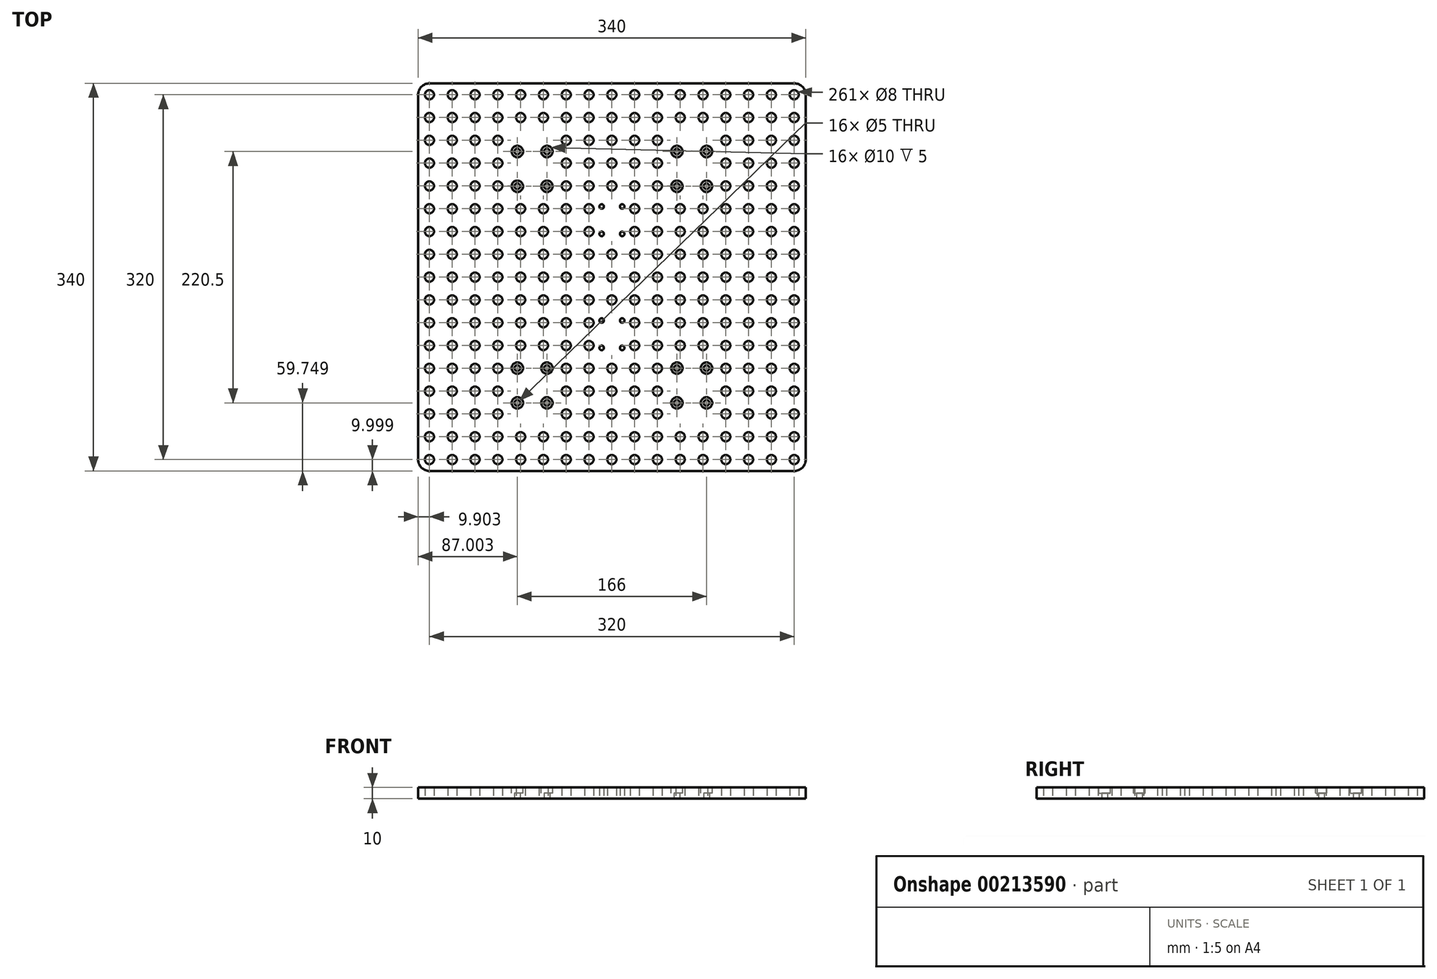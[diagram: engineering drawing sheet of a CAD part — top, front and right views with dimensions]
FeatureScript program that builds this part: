
annotation { "Feature Type Name" : "Feature", "Feature Type Description" : "" }
export const myFeature = defineFeature(function(context is Context, id is Id, definition is map)
    precondition{}
    {
        {
            var Q0;
            Q0=qCreatedBy(makeId("Top.planeOp"),FACE);
            var sketch = newSketch(context, id + "F0", { "sketchPlane" : qUnion([Q0])});
            skLineSegment(sketch, "E0", {"start": v(-202.87, 176.2) * mm, "end": v(-202.87, -163.8) * mm});
            skLineSegment(sketch, "E1", {"start": v(-202.87, -163.8) * mm, "end": v(137.13, -163.8) * mm});
            skLineSegment(sketch, "E2", {"start": v(137.13, -163.8) * mm, "end": v(137.13, 176.2) * mm});
            skLineSegment(sketch, "E3", {"start": v(137.13, 176.2) * mm, "end": v(-202.87, 176.2) * mm});
            skCircle(sketch, "E4", {"center": v(-192.97, -153.8) * mm, "radius": 4 * mm});
            skCircle(sketch, "E5.0.1.0", {"center": v(-192.97, -133.8) * mm, "radius": 4 * mm});
            skCircle(sketch, "E5.0.2.0", {"center": v(-192.97, -113.8) * mm, "radius": 4 * mm});
            skCircle(sketch, "E5.0.3.0", {"center": v(-192.97, -93.8) * mm, "radius": 4 * mm});
            skCircle(sketch, "E5.0.4.0", {"center": v(-192.97, -73.8) * mm, "radius": 4 * mm});
            skCircle(sketch, "E5.0.5.0", {"center": v(-192.97, -53.8) * mm, "radius": 4 * mm});
            skCircle(sketch, "E5.0.6.0", {"center": v(-192.97, -33.8) * mm, "radius": 4 * mm});
            skCircle(sketch, "E5.0.7.0", {"center": v(-192.97, -13.8) * mm, "radius": 4 * mm});
            skCircle(sketch, "E5.0.8.0", {"center": v(-192.97, 6.2) * mm, "radius": 4 * mm});
            skCircle(sketch, "E5.0.9.0", {"center": v(-192.97, 26.2) * mm, "radius": 4 * mm});
            skCircle(sketch, "E5.0.10.0", {"center": v(-192.97, 46.2) * mm, "radius": 4 * mm});
            skCircle(sketch, "E5.0.11.0", {"center": v(-192.97, 66.2) * mm, "radius": 4 * mm});
            skCircle(sketch, "E5.0.12.0", {"center": v(-192.97, 86.2) * mm, "radius": 4 * mm});
            skCircle(sketch, "E5.0.13.0", {"center": v(-192.97, 106.2) * mm, "radius": 4 * mm});
            skCircle(sketch, "E5.0.14.0", {"center": v(-192.97, 126.2) * mm, "radius": 4 * mm});
            skCircle(sketch, "E5.0.15.0", {"center": v(-192.97, 146.2) * mm, "radius": 4 * mm});
            skCircle(sketch, "E5.0.16.0", {"center": v(-192.97, 166.2) * mm, "radius": 4 * mm});
            skLineSegment(sketch, "E5.direction1", {"start": v(-192.97, -153.8) * mm, "end": v(-172.97, -153.8) * mm, "construction": true});
            skLineSegment(sketch, "E5.direction2", {"start": v(-192.97, -153.8) * mm, "end": v(-192.97, -133.8) * mm, "construction": true});
            skCircle(sketch, "E6", {"center": v(24.13, -73.55) * mm, "radius": 2.5 * mm});
            skCircle(sketch, "E7", {"center": v(50.13, -73.55) * mm, "radius": 2.5 * mm});
            skCircle(sketch, "E8", {"center": v(24.13, -104.05) * mm, "radius": 2.5 * mm});
            skCircle(sketch, "E9", {"center": v(50.13, -104.05) * mm, "radius": 2.5 * mm});
            skLineSegment(sketch, "E10", {"start": v(24.13, -73.55) * mm, "end": v(50.13, -104.05) * mm, "construction": true});
            skLineSegment(sketch, "E11", {"start": v(37.13, -88.8) * mm, "end": v(50.13, -104.05) * mm, "construction": true});
            skCircle(sketch, "E12", {"center": v(24.13, 116.45) * mm, "radius": 2.5 * mm});
            skCircle(sketch, "E13", {"center": v(50.13, 116.45) * mm, "radius": 2.5 * mm});
            skCircle(sketch, "E14", {"center": v(24.13, 85.95) * mm, "radius": 2.5 * mm});
            skCircle(sketch, "E15", {"center": v(50.13, 85.95) * mm, "radius": 2.5 * mm});
            skLineSegment(sketch, "E16", {"start": v(24.13, 116.45) * mm, "end": v(50.13, 85.95) * mm, "construction": true});
            skLineSegment(sketch, "E17", {"start": v(37.13, 101.2) * mm, "end": v(50.13, 85.95) * mm, "construction": true});
            skCircle(sketch, "E18", {"center": v(-115.87, 116.45) * mm, "radius": 2.5 * mm});
            skCircle(sketch, "E19", {"center": v(-89.87, 116.45) * mm, "radius": 2.5 * mm});
            skCircle(sketch, "E20", {"center": v(-115.87, 85.95) * mm, "radius": 2.5 * mm});
            skCircle(sketch, "E21", {"center": v(-89.87, 85.95) * mm, "radius": 2.5 * mm});
            skLineSegment(sketch, "E22", {"start": v(-115.87, 116.45) * mm, "end": v(-89.87, 85.95) * mm, "construction": true});
            skLineSegment(sketch, "E23", {"start": v(-102.87, 101.2) * mm, "end": v(-89.87, 85.95) * mm, "construction": true});
            skCircle(sketch, "E24", {"center": v(-115.87, -73.55) * mm, "radius": 2.5 * mm});
            skCircle(sketch, "E25", {"center": v(-89.87, -73.55) * mm, "radius": 2.5 * mm});
            skCircle(sketch, "E26", {"center": v(-115.87, -104.05) * mm, "radius": 2.5 * mm});
            skCircle(sketch, "E27", {"center": v(-89.87, -104.05) * mm, "radius": 2.5 * mm});
            skLineSegment(sketch, "E28", {"start": v(-115.87, -73.55) * mm, "end": v(-89.87, -104.05) * mm, "construction": true});
            skLineSegment(sketch, "E29", {"start": v(-102.87, -88.8) * mm, "end": v(-89.87, -104.05) * mm, "construction": true});
            skCircle(sketch, "E30.0.1.0", {"center": v(-172.97, -153.8) * mm, "radius": 4 * mm});
            skCircle(sketch, "E30.0.1.1", {"center": v(-172.97, -133.8) * mm, "radius": 4 * mm});
            skCircle(sketch, "E30.0.1.2", {"center": v(-172.97, -113.8) * mm, "radius": 4 * mm});
            skCircle(sketch, "E30.0.1.3", {"center": v(-172.97, -93.8) * mm, "radius": 4 * mm});
            skCircle(sketch, "E30.0.1.4", {"center": v(-172.97, -73.8) * mm, "radius": 4 * mm});
            skCircle(sketch, "E30.0.1.5", {"center": v(-172.97, -53.8) * mm, "radius": 4 * mm});
            skCircle(sketch, "E30.0.1.6", {"center": v(-172.97, -33.8) * mm, "radius": 4 * mm});
            skCircle(sketch, "E30.0.1.7", {"center": v(-172.97, -13.8) * mm, "radius": 4 * mm});
            skCircle(sketch, "E30.0.1.8", {"center": v(-172.97, 6.2) * mm, "radius": 4 * mm});
            skCircle(sketch, "E30.0.1.9", {"center": v(-172.97, 26.2) * mm, "radius": 4 * mm});
            skCircle(sketch, "E30.0.1.10", {"center": v(-172.97, 46.2) * mm, "radius": 4 * mm});
            skCircle(sketch, "E30.0.1.11", {"center": v(-172.97, 66.2) * mm, "radius": 4 * mm});
            skCircle(sketch, "E30.0.1.12", {"center": v(-172.97, 86.2) * mm, "radius": 4 * mm});
            skCircle(sketch, "E30.0.1.13", {"center": v(-172.97, 106.2) * mm, "radius": 4 * mm});
            skCircle(sketch, "E30.0.1.14", {"center": v(-172.97, 126.2) * mm, "radius": 4 * mm});
            skCircle(sketch, "E30.0.1.15", {"center": v(-172.97, 146.2) * mm, "radius": 4 * mm});
            skCircle(sketch, "E30.0.1.16", {"center": v(-172.97, 166.2) * mm, "radius": 4 * mm});
            skCircle(sketch, "E30.0.2.0", {"center": v(-152.97, -153.8) * mm, "radius": 4 * mm});
            skCircle(sketch, "E30.0.2.1", {"center": v(-152.97, -133.8) * mm, "radius": 4 * mm});
            skCircle(sketch, "E30.0.2.2", {"center": v(-152.97, -113.8) * mm, "radius": 4 * mm});
            skCircle(sketch, "E30.0.2.3", {"center": v(-152.97, -93.8) * mm, "radius": 4 * mm});
            skCircle(sketch, "E30.0.2.4", {"center": v(-152.97, -73.8) * mm, "radius": 4 * mm});
            skCircle(sketch, "E30.0.2.5", {"center": v(-152.97, -53.8) * mm, "radius": 4 * mm});
            skCircle(sketch, "E30.0.2.6", {"center": v(-152.97, -33.8) * mm, "radius": 4 * mm});
            skCircle(sketch, "E30.0.2.7", {"center": v(-152.97, -13.8) * mm, "radius": 4 * mm});
            skCircle(sketch, "E30.0.2.8", {"center": v(-152.97, 6.2) * mm, "radius": 4 * mm});
            skCircle(sketch, "E30.0.2.9", {"center": v(-152.97, 26.2) * mm, "radius": 4 * mm});
            skCircle(sketch, "E30.0.2.10", {"center": v(-152.97, 46.2) * mm, "radius": 4 * mm});
            skCircle(sketch, "E30.0.2.11", {"center": v(-152.97, 66.2) * mm, "radius": 4 * mm});
            skCircle(sketch, "E30.0.2.12", {"center": v(-152.97, 86.2) * mm, "radius": 4 * mm});
            skCircle(sketch, "E30.0.2.13", {"center": v(-152.97, 106.2) * mm, "radius": 4 * mm});
            skCircle(sketch, "E30.0.2.14", {"center": v(-152.97, 126.2) * mm, "radius": 4 * mm});
            skCircle(sketch, "E30.0.2.15", {"center": v(-152.97, 146.2) * mm, "radius": 4 * mm});
            skCircle(sketch, "E30.0.2.16", {"center": v(-152.97, 166.2) * mm, "radius": 4 * mm});
            skCircle(sketch, "E30.0.3.0", {"center": v(-132.97, -153.8) * mm, "radius": 4 * mm});
            skCircle(sketch, "E30.0.3.1", {"center": v(-132.97, -133.8) * mm, "radius": 4 * mm});
            skCircle(sketch, "E30.0.3.2", {"center": v(-132.97, -113.8) * mm, "radius": 4 * mm});
            skCircle(sketch, "E30.0.3.3", {"center": v(-132.97, -93.8) * mm, "radius": 4 * mm});
            skCircle(sketch, "E30.0.3.4", {"center": v(-132.97, -73.8) * mm, "radius": 4 * mm});
            skCircle(sketch, "E30.0.3.5", {"center": v(-132.97, -53.8) * mm, "radius": 4 * mm});
            skCircle(sketch, "E30.0.3.6", {"center": v(-132.97, -33.8) * mm, "radius": 4 * mm});
            skCircle(sketch, "E30.0.3.7", {"center": v(-132.97, -13.8) * mm, "radius": 4 * mm});
            skCircle(sketch, "E30.0.3.8", {"center": v(-132.97, 6.2) * mm, "radius": 4 * mm});
            skCircle(sketch, "E30.0.3.9", {"center": v(-132.97, 26.2) * mm, "radius": 4 * mm});
            skCircle(sketch, "E30.0.3.10", {"center": v(-132.97, 46.2) * mm, "radius": 4 * mm});
            skCircle(sketch, "E30.0.3.11", {"center": v(-132.97, 66.2) * mm, "radius": 4 * mm});
            skCircle(sketch, "E30.0.3.12", {"center": v(-132.97, 86.2) * mm, "radius": 4 * mm});
            skCircle(sketch, "E30.0.3.13", {"center": v(-132.97, 106.2) * mm, "radius": 4 * mm});
            skCircle(sketch, "E30.0.3.14", {"center": v(-132.97, 126.2) * mm, "radius": 4 * mm});
            skCircle(sketch, "E30.0.3.15", {"center": v(-132.97, 146.2) * mm, "radius": 4 * mm});
            skCircle(sketch, "E30.0.3.16", {"center": v(-132.97, 166.2) * mm, "radius": 4 * mm});
            skCircle(sketch, "E30.0.4.0", {"center": v(-112.97, -153.8) * mm, "radius": 4 * mm});
            skCircle(sketch, "E30.0.4.1", {"center": v(-112.97, -133.8) * mm, "radius": 4 * mm});
            skCircle(sketch, "E30.0.4.5", {"center": v(-112.97, -53.8) * mm, "radius": 4 * mm});
            skCircle(sketch, "E30.0.4.6", {"center": v(-112.97, -33.8) * mm, "radius": 4 * mm});
            skCircle(sketch, "E30.0.4.7", {"center": v(-112.97, -13.8) * mm, "radius": 4 * mm});
            skCircle(sketch, "E30.0.4.8", {"center": v(-112.97, 6.2) * mm, "radius": 4 * mm});
            skCircle(sketch, "E30.0.4.9", {"center": v(-112.97, 26.2) * mm, "radius": 4 * mm});
            skCircle(sketch, "E30.0.4.10", {"center": v(-112.97, 46.2) * mm, "radius": 4 * mm});
            skCircle(sketch, "E30.0.4.11", {"center": v(-112.97, 66.2) * mm, "radius": 4 * mm});
            skCircle(sketch, "E30.0.4.15", {"center": v(-112.97, 146.2) * mm, "radius": 4 * mm});
            skCircle(sketch, "E30.0.4.16", {"center": v(-112.97, 166.2) * mm, "radius": 4 * mm});
            skCircle(sketch, "E30.0.5.0", {"center": v(-92.97, -153.8) * mm, "radius": 4 * mm});
            skCircle(sketch, "E30.0.5.1", {"center": v(-92.97, -133.8) * mm, "radius": 4 * mm});
            skCircle(sketch, "E30.0.5.5", {"center": v(-92.97, -53.8) * mm, "radius": 4 * mm});
            skCircle(sketch, "E30.0.5.6", {"center": v(-92.97, -33.8) * mm, "radius": 4 * mm});
            skCircle(sketch, "E30.0.5.7", {"center": v(-92.97, -13.8) * mm, "radius": 4 * mm});
            skCircle(sketch, "E30.0.5.8", {"center": v(-92.97, 6.2) * mm, "radius": 4 * mm});
            skCircle(sketch, "E30.0.5.9", {"center": v(-92.97, 26.2) * mm, "radius": 4 * mm});
            skCircle(sketch, "E30.0.5.10", {"center": v(-92.97, 46.2) * mm, "radius": 4 * mm});
            skCircle(sketch, "E30.0.5.11", {"center": v(-92.97, 66.2) * mm, "radius": 4 * mm});
            skCircle(sketch, "E30.0.5.15", {"center": v(-92.97, 146.2) * mm, "radius": 4 * mm});
            skCircle(sketch, "E30.0.5.16", {"center": v(-92.97, 166.2) * mm, "radius": 4 * mm});
            skCircle(sketch, "E30.0.6.0", {"center": v(-72.97, -153.8) * mm, "radius": 4 * mm});
            skCircle(sketch, "E30.0.6.1", {"center": v(-72.97, -133.8) * mm, "radius": 4 * mm});
            skCircle(sketch, "E30.0.6.2", {"center": v(-72.97, -113.8) * mm, "radius": 4 * mm});
            skCircle(sketch, "E30.0.6.3", {"center": v(-72.97, -93.8) * mm, "radius": 4 * mm});
            skCircle(sketch, "E30.0.6.4", {"center": v(-72.97, -73.8) * mm, "radius": 4 * mm});
            skCircle(sketch, "E30.0.6.5", {"center": v(-72.97, -53.8) * mm, "radius": 4 * mm});
            skCircle(sketch, "E30.0.6.6", {"center": v(-72.97, -33.8) * mm, "radius": 4 * mm});
            skCircle(sketch, "E30.0.6.7", {"center": v(-72.97, -13.8) * mm, "radius": 4 * mm});
            skCircle(sketch, "E30.0.6.8", {"center": v(-72.97, 6.2) * mm, "radius": 4 * mm});
            skCircle(sketch, "E30.0.6.9", {"center": v(-72.97, 26.2) * mm, "radius": 4 * mm});
            skCircle(sketch, "E30.0.6.10", {"center": v(-72.97, 46.2) * mm, "radius": 4 * mm});
            skCircle(sketch, "E30.0.6.11", {"center": v(-72.97, 66.2) * mm, "radius": 4 * mm});
            skCircle(sketch, "E30.0.6.12", {"center": v(-72.97, 86.2) * mm, "radius": 4 * mm});
            skCircle(sketch, "E30.0.6.13", {"center": v(-72.97, 106.2) * mm, "radius": 4 * mm});
            skCircle(sketch, "E30.0.6.14", {"center": v(-72.97, 126.2) * mm, "radius": 4 * mm});
            skCircle(sketch, "E30.0.6.15", {"center": v(-72.97, 146.2) * mm, "radius": 4 * mm});
            skCircle(sketch, "E30.0.6.16", {"center": v(-72.97, 166.2) * mm, "radius": 4 * mm});
            skCircle(sketch, "E30.0.7.0", {"center": v(-52.97, -153.8) * mm, "radius": 4 * mm});
            skCircle(sketch, "E30.0.7.1", {"center": v(-52.97, -133.8) * mm, "radius": 4 * mm});
            skCircle(sketch, "E30.0.7.2", {"center": v(-52.97, -113.8) * mm, "radius": 4 * mm});
            skCircle(sketch, "E30.0.7.3", {"center": v(-52.97, -93.8) * mm, "radius": 4 * mm});
            skCircle(sketch, "E30.0.7.4", {"center": v(-52.97, -73.8) * mm, "radius": 4 * mm});
            skCircle(sketch, "E30.0.7.5", {"center": v(-52.97, -53.8) * mm, "radius": 4 * mm});
            skCircle(sketch, "E30.0.7.6", {"center": v(-52.97, -33.8) * mm, "radius": 4 * mm});
            skCircle(sketch, "E30.0.7.7", {"center": v(-52.97, -13.8) * mm, "radius": 4 * mm});
            skCircle(sketch, "E30.0.7.8", {"center": v(-52.97, 6.2) * mm, "radius": 4 * mm});
            skCircle(sketch, "E30.0.7.9", {"center": v(-52.97, 26.2) * mm, "radius": 4 * mm});
            skCircle(sketch, "E30.0.7.10", {"center": v(-52.97, 46.2) * mm, "radius": 4 * mm});
            skCircle(sketch, "E30.0.7.11", {"center": v(-52.97, 66.2) * mm, "radius": 4 * mm});
            skCircle(sketch, "E30.0.7.12", {"center": v(-52.97, 86.2) * mm, "radius": 4 * mm});
            skCircle(sketch, "E30.0.7.13", {"center": v(-52.97, 106.2) * mm, "radius": 4 * mm});
            skCircle(sketch, "E30.0.7.14", {"center": v(-52.97, 126.2) * mm, "radius": 4 * mm});
            skCircle(sketch, "E30.0.7.15", {"center": v(-52.97, 146.2) * mm, "radius": 4 * mm});
            skCircle(sketch, "E30.0.7.16", {"center": v(-52.97, 166.2) * mm, "radius": 4 * mm});
            skCircle(sketch, "E30.0.8.0", {"center": v(-32.97, -153.8) * mm, "radius": 4 * mm});
            skCircle(sketch, "E30.0.8.1", {"center": v(-32.97, -133.8) * mm, "radius": 4 * mm});
            skCircle(sketch, "E30.0.8.2", {"center": v(-32.97, -113.8) * mm, "radius": 4 * mm});
            skCircle(sketch, "E30.0.8.3", {"center": v(-32.97, -93.8) * mm, "radius": 4 * mm});
            skCircle(sketch, "E30.0.8.4", {"center": v(-32.97, -73.8) * mm, "radius": 4 * mm});
            skCircle(sketch, "E30.0.8.7", {"center": v(-32.97, -13.8) * mm, "radius": 4 * mm});
            skCircle(sketch, "E30.0.8.8", {"center": v(-32.97, 6.2) * mm, "radius": 4 * mm});
            skCircle(sketch, "E30.0.8.9", {"center": v(-32.97, 26.2) * mm, "radius": 4 * mm});
            skCircle(sketch, "E30.0.8.12", {"center": v(-32.97, 86.2) * mm, "radius": 4 * mm});
            skCircle(sketch, "E30.0.8.13", {"center": v(-32.97, 106.2) * mm, "radius": 4 * mm});
            skCircle(sketch, "E30.0.8.14", {"center": v(-32.97, 126.2) * mm, "radius": 4 * mm});
            skCircle(sketch, "E30.0.8.15", {"center": v(-32.97, 146.2) * mm, "radius": 4 * mm});
            skCircle(sketch, "E30.0.8.16", {"center": v(-32.97, 166.2) * mm, "radius": 4 * mm});
            skCircle(sketch, "E30.0.9.0", {"center": v(-12.97, -153.8) * mm, "radius": 4 * mm});
            skCircle(sketch, "E30.0.9.1", {"center": v(-12.97, -133.8) * mm, "radius": 4 * mm});
            skCircle(sketch, "E30.0.9.2", {"center": v(-12.97, -113.8) * mm, "radius": 4 * mm});
            skCircle(sketch, "E30.0.9.3", {"center": v(-12.97, -93.8) * mm, "radius": 4 * mm});
            skCircle(sketch, "E30.0.9.4", {"center": v(-12.97, -73.8) * mm, "radius": 4 * mm});
            skCircle(sketch, "E30.0.9.5", {"center": v(-12.97, -53.8) * mm, "radius": 4 * mm});
            skCircle(sketch, "E30.0.9.6", {"center": v(-12.97, -33.8) * mm, "radius": 4 * mm});
            skCircle(sketch, "E30.0.9.7", {"center": v(-12.97, -13.8) * mm, "radius": 4 * mm});
            skCircle(sketch, "E30.0.9.8", {"center": v(-12.97, 6.2) * mm, "radius": 4 * mm});
            skCircle(sketch, "E30.0.9.9", {"center": v(-12.97, 26.2) * mm, "radius": 4 * mm});
            skCircle(sketch, "E30.0.9.10", {"center": v(-12.97, 46.2) * mm, "radius": 4 * mm});
            skCircle(sketch, "E30.0.9.11", {"center": v(-12.97, 66.2) * mm, "radius": 4 * mm});
            skCircle(sketch, "E30.0.9.12", {"center": v(-12.97, 86.2) * mm, "radius": 4 * mm});
            skCircle(sketch, "E30.0.9.13", {"center": v(-12.97, 106.2) * mm, "radius": 4 * mm});
            skCircle(sketch, "E30.0.9.14", {"center": v(-12.97, 126.2) * mm, "radius": 4 * mm});
            skCircle(sketch, "E30.0.9.15", {"center": v(-12.97, 146.2) * mm, "radius": 4 * mm});
            skCircle(sketch, "E30.0.9.16", {"center": v(-12.97, 166.2) * mm, "radius": 4 * mm});
            skCircle(sketch, "E30.0.10.0", {"center": v(7.03, -153.8) * mm, "radius": 4 * mm});
            skCircle(sketch, "E30.0.10.1", {"center": v(7.03, -133.8) * mm, "radius": 4 * mm});
            skCircle(sketch, "E30.0.10.2", {"center": v(7.03, -113.8) * mm, "radius": 4 * mm});
            skCircle(sketch, "E30.0.10.3", {"center": v(7.03, -93.8) * mm, "radius": 4 * mm});
            skCircle(sketch, "E30.0.10.4", {"center": v(7.03, -73.8) * mm, "radius": 4 * mm});
            skCircle(sketch, "E30.0.10.5", {"center": v(7.03, -53.8) * mm, "radius": 4 * mm});
            skCircle(sketch, "E30.0.10.6", {"center": v(7.03, -33.8) * mm, "radius": 4 * mm});
            skCircle(sketch, "E30.0.10.7", {"center": v(7.03, -13.8) * mm, "radius": 4 * mm});
            skCircle(sketch, "E30.0.10.8", {"center": v(7.03, 6.2) * mm, "radius": 4 * mm});
            skCircle(sketch, "E30.0.10.9", {"center": v(7.03, 26.2) * mm, "radius": 4 * mm});
            skCircle(sketch, "E30.0.10.10", {"center": v(7.03, 46.2) * mm, "radius": 4 * mm});
            skCircle(sketch, "E30.0.10.11", {"center": v(7.03, 66.2) * mm, "radius": 4 * mm});
            skCircle(sketch, "E30.0.10.12", {"center": v(7.03, 86.2) * mm, "radius": 4 * mm});
            skCircle(sketch, "E30.0.10.13", {"center": v(7.03, 106.2) * mm, "radius": 4 * mm});
            skCircle(sketch, "E30.0.10.14", {"center": v(7.03, 126.2) * mm, "radius": 4 * mm});
            skCircle(sketch, "E30.0.10.15", {"center": v(7.03, 146.2) * mm, "radius": 4 * mm});
            skCircle(sketch, "E30.0.10.16", {"center": v(7.03, 166.2) * mm, "radius": 4 * mm});
            skCircle(sketch, "E30.0.11.0", {"center": v(27.03, -153.8) * mm, "radius": 4 * mm});
            skCircle(sketch, "E30.0.11.1", {"center": v(27.03, -133.8) * mm, "radius": 4 * mm});
            skCircle(sketch, "E30.0.11.5", {"center": v(27.03, -53.8) * mm, "radius": 4 * mm});
            skCircle(sketch, "E30.0.11.6", {"center": v(27.03, -33.8) * mm, "radius": 4 * mm});
            skCircle(sketch, "E30.0.11.7", {"center": v(27.03, -13.8) * mm, "radius": 4 * mm});
            skCircle(sketch, "E30.0.11.8", {"center": v(27.03, 6.2) * mm, "radius": 4 * mm});
            skCircle(sketch, "E30.0.11.9", {"center": v(27.03, 26.2) * mm, "radius": 4 * mm});
            skCircle(sketch, "E30.0.11.10", {"center": v(27.03, 46.2) * mm, "radius": 4 * mm});
            skCircle(sketch, "E30.0.11.11", {"center": v(27.03, 66.2) * mm, "radius": 4 * mm});
            skCircle(sketch, "E30.0.11.15", {"center": v(27.03, 146.2) * mm, "radius": 4 * mm});
            skCircle(sketch, "E30.0.11.16", {"center": v(27.03, 166.2) * mm, "radius": 4 * mm});
            skCircle(sketch, "E30.0.12.0", {"center": v(47.03, -153.8) * mm, "radius": 4 * mm});
            skCircle(sketch, "E30.0.12.1", {"center": v(47.03, -133.8) * mm, "radius": 4 * mm});
            skCircle(sketch, "E30.0.12.5", {"center": v(47.03, -53.8) * mm, "radius": 4 * mm});
            skCircle(sketch, "E30.0.12.6", {"center": v(47.03, -33.8) * mm, "radius": 4 * mm});
            skCircle(sketch, "E30.0.12.7", {"center": v(47.03, -13.8) * mm, "radius": 4 * mm});
            skCircle(sketch, "E30.0.12.8", {"center": v(47.03, 6.2) * mm, "radius": 4 * mm});
            skCircle(sketch, "E30.0.12.9", {"center": v(47.03, 26.2) * mm, "radius": 4 * mm});
            skCircle(sketch, "E30.0.12.10", {"center": v(47.03, 46.2) * mm, "radius": 4 * mm});
            skCircle(sketch, "E30.0.12.11", {"center": v(47.03, 66.2) * mm, "radius": 4 * mm});
            skCircle(sketch, "E30.0.12.15", {"center": v(47.03, 146.2) * mm, "radius": 4 * mm});
            skCircle(sketch, "E30.0.12.16", {"center": v(47.03, 166.2) * mm, "radius": 4 * mm});
            skCircle(sketch, "E30.0.13.0", {"center": v(67.03, -153.8) * mm, "radius": 4 * mm});
            skCircle(sketch, "E30.0.13.1", {"center": v(67.03, -133.8) * mm, "radius": 4 * mm});
            skCircle(sketch, "E30.0.13.2", {"center": v(67.03, -113.8) * mm, "radius": 4 * mm});
            skCircle(sketch, "E30.0.13.3", {"center": v(67.03, -93.8) * mm, "radius": 4 * mm});
            skCircle(sketch, "E30.0.13.4", {"center": v(67.03, -73.8) * mm, "radius": 4 * mm});
            skCircle(sketch, "E30.0.13.5", {"center": v(67.03, -53.8) * mm, "radius": 4 * mm});
            skCircle(sketch, "E30.0.13.6", {"center": v(67.03, -33.8) * mm, "radius": 4 * mm});
            skCircle(sketch, "E30.0.13.7", {"center": v(67.03, -13.8) * mm, "radius": 4 * mm});
            skCircle(sketch, "E30.0.13.8", {"center": v(67.03, 6.2) * mm, "radius": 4 * mm});
            skCircle(sketch, "E30.0.13.9", {"center": v(67.03, 26.2) * mm, "radius": 4 * mm});
            skCircle(sketch, "E30.0.13.10", {"center": v(67.03, 46.2) * mm, "radius": 4 * mm});
            skCircle(sketch, "E30.0.13.11", {"center": v(67.03, 66.2) * mm, "radius": 4 * mm});
            skCircle(sketch, "E30.0.13.12", {"center": v(67.03, 86.2) * mm, "radius": 4 * mm});
            skCircle(sketch, "E30.0.13.13", {"center": v(67.03, 106.2) * mm, "radius": 4 * mm});
            skCircle(sketch, "E30.0.13.14", {"center": v(67.03, 126.2) * mm, "radius": 4 * mm});
            skCircle(sketch, "E30.0.13.15", {"center": v(67.03, 146.2) * mm, "radius": 4 * mm});
            skCircle(sketch, "E30.0.13.16", {"center": v(67.03, 166.2) * mm, "radius": 4 * mm});
            skCircle(sketch, "E30.0.14.0", {"center": v(87.03, -153.8) * mm, "radius": 4 * mm});
            skCircle(sketch, "E30.0.14.1", {"center": v(87.03, -133.8) * mm, "radius": 4 * mm});
            skCircle(sketch, "E30.0.14.2", {"center": v(87.03, -113.8) * mm, "radius": 4 * mm});
            skCircle(sketch, "E30.0.14.3", {"center": v(87.03, -93.8) * mm, "radius": 4 * mm});
            skCircle(sketch, "E30.0.14.4", {"center": v(87.03, -73.8) * mm, "radius": 4 * mm});
            skCircle(sketch, "E30.0.14.5", {"center": v(87.03, -53.8) * mm, "radius": 4 * mm});
            skCircle(sketch, "E30.0.14.6", {"center": v(87.03, -33.8) * mm, "radius": 4 * mm});
            skCircle(sketch, "E30.0.14.7", {"center": v(87.03, -13.8) * mm, "radius": 4 * mm});
            skCircle(sketch, "E30.0.14.8", {"center": v(87.03, 6.2) * mm, "radius": 4 * mm});
            skCircle(sketch, "E30.0.14.9", {"center": v(87.03, 26.2) * mm, "radius": 4 * mm});
            skCircle(sketch, "E30.0.14.10", {"center": v(87.03, 46.2) * mm, "radius": 4 * mm});
            skCircle(sketch, "E30.0.14.11", {"center": v(87.03, 66.2) * mm, "radius": 4 * mm});
            skCircle(sketch, "E30.0.14.12", {"center": v(87.03, 86.2) * mm, "radius": 4 * mm});
            skCircle(sketch, "E30.0.14.13", {"center": v(87.03, 106.2) * mm, "radius": 4 * mm});
            skCircle(sketch, "E30.0.14.14", {"center": v(87.03, 126.2) * mm, "radius": 4 * mm});
            skCircle(sketch, "E30.0.14.15", {"center": v(87.03, 146.2) * mm, "radius": 4 * mm});
            skCircle(sketch, "E30.0.14.16", {"center": v(87.03, 166.2) * mm, "radius": 4 * mm});
            skCircle(sketch, "E30.0.15.0", {"center": v(107.03, -153.8) * mm, "radius": 4 * mm});
            skCircle(sketch, "E30.0.15.1", {"center": v(107.03, -133.8) * mm, "radius": 4 * mm});
            skCircle(sketch, "E30.0.15.2", {"center": v(107.03, -113.8) * mm, "radius": 4 * mm});
            skCircle(sketch, "E30.0.15.3", {"center": v(107.03, -93.8) * mm, "radius": 4 * mm});
            skCircle(sketch, "E30.0.15.4", {"center": v(107.03, -73.8) * mm, "radius": 4 * mm});
            skCircle(sketch, "E30.0.15.5", {"center": v(107.03, -53.8) * mm, "radius": 4 * mm});
            skCircle(sketch, "E30.0.15.6", {"center": v(107.03, -33.8) * mm, "radius": 4 * mm});
            skCircle(sketch, "E30.0.15.7", {"center": v(107.03, -13.8) * mm, "radius": 4 * mm});
            skCircle(sketch, "E30.0.15.8", {"center": v(107.03, 6.2) * mm, "radius": 4 * mm});
            skCircle(sketch, "E30.0.15.9", {"center": v(107.03, 26.2) * mm, "radius": 4 * mm});
            skCircle(sketch, "E30.0.15.10", {"center": v(107.03, 46.2) * mm, "radius": 4 * mm});
            skCircle(sketch, "E30.0.15.11", {"center": v(107.03, 66.2) * mm, "radius": 4 * mm});
            skCircle(sketch, "E30.0.15.12", {"center": v(107.03, 86.2) * mm, "radius": 4 * mm});
            skCircle(sketch, "E30.0.15.13", {"center": v(107.03, 106.2) * mm, "radius": 4 * mm});
            skCircle(sketch, "E30.0.15.14", {"center": v(107.03, 126.2) * mm, "radius": 4 * mm});
            skCircle(sketch, "E30.0.15.15", {"center": v(107.03, 146.2) * mm, "radius": 4 * mm});
            skCircle(sketch, "E30.0.15.16", {"center": v(107.03, 166.2) * mm, "radius": 4 * mm});
            skCircle(sketch, "E30.0.16.0", {"center": v(127.03, -153.8) * mm, "radius": 4 * mm});
            skCircle(sketch, "E30.0.16.1", {"center": v(127.03, -133.8) * mm, "radius": 4 * mm});
            skCircle(sketch, "E30.0.16.2", {"center": v(127.03, -113.8) * mm, "radius": 4 * mm});
            skCircle(sketch, "E30.0.16.3", {"center": v(127.03, -93.8) * mm, "radius": 4 * mm});
            skCircle(sketch, "E30.0.16.4", {"center": v(127.03, -73.8) * mm, "radius": 4 * mm});
            skCircle(sketch, "E30.0.16.5", {"center": v(127.03, -53.8) * mm, "radius": 4 * mm});
            skCircle(sketch, "E30.0.16.6", {"center": v(127.03, -33.8) * mm, "radius": 4 * mm});
            skCircle(sketch, "E30.0.16.7", {"center": v(127.03, -13.8) * mm, "radius": 4 * mm});
            skCircle(sketch, "E30.0.16.8", {"center": v(127.03, 6.2) * mm, "radius": 4 * mm});
            skCircle(sketch, "E30.0.16.9", {"center": v(127.03, 26.2) * mm, "radius": 4 * mm});
            skCircle(sketch, "E30.0.16.10", {"center": v(127.03, 46.2) * mm, "radius": 4 * mm});
            skCircle(sketch, "E30.0.16.11", {"center": v(127.03, 66.2) * mm, "radius": 4 * mm});
            skCircle(sketch, "E30.0.16.12", {"center": v(127.03, 86.2) * mm, "radius": 4 * mm});
            skCircle(sketch, "E30.0.16.13", {"center": v(127.03, 106.2) * mm, "radius": 4 * mm});
            skCircle(sketch, "E30.0.16.14", {"center": v(127.03, 126.2) * mm, "radius": 4 * mm});
            skCircle(sketch, "E30.0.16.15", {"center": v(127.03, 146.2) * mm, "radius": 4 * mm});
            skCircle(sketch, "E30.0.16.16", {"center": v(127.03, 166.2) * mm, "radius": 4 * mm});
            skCircle(sketch, "E31", {"center": v(-41.87, -55.8) * mm, "radius": 2 * mm});
            skCircle(sketch, "E32", {"center": v(-23.87, -55.8) * mm, "radius": 2 * mm});
            skCircle(sketch, "E33", {"center": v(-23.87, -31.8) * mm, "radius": 2 * mm});
            skCircle(sketch, "E34", {"center": v(-41.87, -31.8) * mm, "radius": 2 * mm});
            skCircle(sketch, "E35", {"center": v(-41.87, 44.2) * mm, "radius": 2 * mm});
            skCircle(sketch, "E36", {"center": v(-41.87, 68.2) * mm, "radius": 2 * mm});
            skCircle(sketch, "E37", {"center": v(-23.87, 44.2) * mm, "radius": 2 * mm});
            skCircle(sketch, "E38", {"center": v(-23.87, 68.2) * mm, "radius": 2 * mm});
            skSolve(sketch);
        }
        {
            var Q0;
            Q0=makeQuery(id+"F0.imprint","IMPRINT",FACE,{"disambiguationData":[TD([[makeQuery(id+"F0.imprint","IMPRINT",EDGE,{"derivedFrom":sQuery(id+"F0.wireOp",EDGE,"E0")}),1.0]])]});
            extrude(context, id + "F1", {"entities" : qUnion([Q0]), "depth" : 10 * mm});
        }
        {
            var Q0;
            Q0=makeQuery(id+"F1.opExtrude","SWEPT_EDGE",EDGE,{"disambiguationData":[OSD([sQuery(id+"F0.wireOp",EDGE,"E1"),sQuery(id+"F0.wireOp",EDGE,"E2")])]});
            var Q1;
            Q1=makeQuery(id+"F1.opExtrude","SWEPT_EDGE",EDGE,{"disambiguationData":[OSD([sQuery(id+"F0.wireOp",EDGE,"E0"),sQuery(id+"F0.wireOp",EDGE,"E1")])]});
            var Q2;
            Q2=makeQuery(id+"F1.opExtrude","SWEPT_EDGE",EDGE,{"disambiguationData":[OSD([sQuery(id+"F0.wireOp",EDGE,"E0"),sQuery(id+"F0.wireOp",EDGE,"E3")])]});
            var Q3;
            Q3=makeQuery(id+"F1.opExtrude","SWEPT_EDGE",EDGE,{"disambiguationData":[OSD([sQuery(id+"F0.wireOp",EDGE,"E2"),sQuery(id+"F0.wireOp",EDGE,"E3")])]});
            fillet(context, id + "F2", {"entities" : qUnion([Q0, Q1, Q2, Q3]), "radius" : 10 * mm, "tangentPropagation" : true, "allowEdgeOverflow" : false});
        }
        {
            var Q0;
            Q0=makeQuery(id+"F1.opExtrude","CAP_FACE",FACE,{"disambiguationData":[OSD([sQuery(id+"F0.wireOp",EDGE,"E0"),sQuery(id+"F0.wireOp",EDGE,"E1"),sQuery(id+"F0.wireOp",EDGE,"E2"),sQuery(id+"F0.wireOp",EDGE,"E3"),sQuery(id+"F0.wireOp",EDGE,"E4"),sQuery(id+"F0.wireOp",EDGE,"E5.0.1.0"),sQuery(id+"F0.wireOp",EDGE,"E5.0.2.0"),sQuery(id+"F0.wireOp",EDGE,"E5.0.3.0"),sQuery(id+"F0.wireOp",EDGE,"E5.0.4.0"),sQuery(id+"F0.wireOp",EDGE,"E5.0.5.0"),sQuery(id+"F0.wireOp",EDGE,"E5.0.6.0"),sQuery(id+"F0.wireOp",EDGE,"E5.0.7.0"),sQuery(id+"F0.wireOp",EDGE,"E5.0.8.0"),sQuery(id+"F0.wireOp",EDGE,"E5.0.9.0"),sQuery(id+"F0.wireOp",EDGE,"E5.0.10.0"),sQuery(id+"F0.wireOp",EDGE,"E5.0.11.0"),sQuery(id+"F0.wireOp",EDGE,"E5.0.12.0"),sQuery(id+"F0.wireOp",EDGE,"E5.0.13.0"),sQuery(id+"F0.wireOp",EDGE,"E5.0.14.0"),sQuery(id+"F0.wireOp",EDGE,"E5.0.15.0"),sQuery(id+"F0.wireOp",EDGE,"E5.0.16.0"),sQuery(id+"F0.wireOp",EDGE,"E5.0.17.0"),sQuery(id+"F0.wireOp",EDGE,"E5.0.18.0"),sQuery(id+"F0.wireOp",EDGE,"E5.1.0.0"),sQuery(id+"F0.wireOp",EDGE,"E5.1.1.0"),sQuery(id+"F0.wireOp",EDGE,"E5.1.2.0"),sQuery(id+"F0.wireOp",EDGE,"E5.1.3.0"),sQuery(id+"F0.wireOp",EDGE,"E5.1.4.0"),sQuery(id+"F0.wireOp",EDGE,"E5.1.5.0"),sQuery(id+"F0.wireOp",EDGE,"E5.1.6.0"),sQuery(id+"F0.wireOp",EDGE,"E5.1.7.0"),sQuery(id+"F0.wireOp",EDGE,"E5.1.8.0"),sQuery(id+"F0.wireOp",EDGE,"E5.1.9.0"),sQuery(id+"F0.wireOp",EDGE,"E5.1.10.0"),sQuery(id+"F0.wireOp",EDGE,"E5.1.11.0"),sQuery(id+"F0.wireOp",EDGE,"E5.1.12.0"),sQuery(id+"F0.wireOp",EDGE,"E5.1.13.0"),sQuery(id+"F0.wireOp",EDGE,"E5.1.14.0"),sQuery(id+"F0.wireOp",EDGE,"E5.1.15.0"),sQuery(id+"F0.wireOp",EDGE,"E5.1.16.0"),sQuery(id+"F0.wireOp",EDGE,"E5.1.17.0"),sQuery(id+"F0.wireOp",EDGE,"E5.1.18.0"),sQuery(id+"F0.wireOp",EDGE,"E5.2.0.0"),sQuery(id+"F0.wireOp",EDGE,"E5.2.1.0"),sQuery(id+"F0.wireOp",EDGE,"E5.2.2.0"),sQuery(id+"F0.wireOp",EDGE,"E5.2.3.0"),sQuery(id+"F0.wireOp",EDGE,"E5.2.4.0"),sQuery(id+"F0.wireOp",EDGE,"E5.2.5.0"),sQuery(id+"F0.wireOp",EDGE,"E5.2.6.0"),sQuery(id+"F0.wireOp",EDGE,"E5.2.7.0"),sQuery(id+"F0.wireOp",EDGE,"E5.2.8.0"),sQuery(id+"F0.wireOp",EDGE,"E5.2.9.0"),sQuery(id+"F0.wireOp",EDGE,"E5.2.10.0"),sQuery(id+"F0.wireOp",EDGE,"E5.2.11.0"),sQuery(id+"F0.wireOp",EDGE,"E5.2.12.0"),sQuery(id+"F0.wireOp",EDGE,"E5.2.13.0"),sQuery(id+"F0.wireOp",EDGE,"E5.2.14.0"),sQuery(id+"F0.wireOp",EDGE,"E5.2.15.0"),sQuery(id+"F0.wireOp",EDGE,"E5.2.16.0"),sQuery(id+"F0.wireOp",EDGE,"E5.2.17.0"),sQuery(id+"F0.wireOp",EDGE,"E5.2.18.0"),sQuery(id+"F0.wireOp",EDGE,"E5.3.0.0"),sQuery(id+"F0.wireOp",EDGE,"E5.3.1.0"),sQuery(id+"F0.wireOp",EDGE,"E5.3.2.0"),sQuery(id+"F0.wireOp",EDGE,"E5.3.3.0"),sQuery(id+"F0.wireOp",EDGE,"E5.3.4.0"),sQuery(id+"F0.wireOp",EDGE,"E5.3.5.0"),sQuery(id+"F0.wireOp",EDGE,"E5.3.6.0"),sQuery(id+"F0.wireOp",EDGE,"E5.3.7.0"),sQuery(id+"F0.wireOp",EDGE,"E5.3.8.0"),sQuery(id+"F0.wireOp",EDGE,"E5.3.9.0"),sQuery(id+"F0.wireOp",EDGE,"E5.3.10.0"),sQuery(id+"F0.wireOp",EDGE,"E5.3.11.0"),sQuery(id+"F0.wireOp",EDGE,"E5.3.12.0"),sQuery(id+"F0.wireOp",EDGE,"E5.3.13.0"),sQuery(id+"F0.wireOp",EDGE,"E5.3.14.0"),sQuery(id+"F0.wireOp",EDGE,"E5.3.15.0"),sQuery(id+"F0.wireOp",EDGE,"E5.3.16.0"),sQuery(id+"F0.wireOp",EDGE,"E5.3.17.0"),sQuery(id+"F0.wireOp",EDGE,"E5.3.18.0"),sQuery(id+"F0.wireOp",EDGE,"E5.4.0.0"),sQuery(id+"F0.wireOp",EDGE,"E5.4.1.0"),sQuery(id+"F0.wireOp",EDGE,"E5.4.2.0"),sQuery(id+"F0.wireOp",EDGE,"E5.4.3.0"),sQuery(id+"F0.wireOp",EDGE,"E5.4.7.0"),sQuery(id+"F0.wireOp",EDGE,"E5.4.8.0"),sQuery(id+"F0.wireOp",EDGE,"E5.4.9.0"),sQuery(id+"F0.wireOp",EDGE,"E5.4.10.0"),sQuery(id+"F0.wireOp",EDGE,"E5.4.11.0"),sQuery(id+"F0.wireOp",EDGE,"E5.4.12.0"),sQuery(id+"F0.wireOp",EDGE,"E5.4.16.0"),sQuery(id+"F0.wireOp",EDGE,"E5.4.17.0"),sQuery(id+"F0.wireOp",EDGE,"E5.4.18.0"),sQuery(id+"F0.wireOp",EDGE,"E5.5.0.0"),sQuery(id+"F0.wireOp",EDGE,"E5.5.1.0"),sQuery(id+"F0.wireOp",EDGE,"E5.5.2.0"),sQuery(id+"F0.wireOp",EDGE,"E5.5.3.0"),sQuery(id+"F0.wireOp",EDGE,"E5.5.7.0"),sQuery(id+"F0.wireOp",EDGE,"E5.5.8.0"),sQuery(id+"F0.wireOp",EDGE,"E5.5.9.0"),sQuery(id+"F0.wireOp",EDGE,"E5.5.10.0"),sQuery(id+"F0.wireOp",EDGE,"E5.5.11.0"),sQuery(id+"F0.wireOp",EDGE,"E5.5.12.0"),sQuery(id+"F0.wireOp",EDGE,"E5.5.16.0"),sQuery(id+"F0.wireOp",EDGE,"E5.5.17.0"),sQuery(id+"F0.wireOp",EDGE,"E5.5.18.0"),sQuery(id+"F0.wireOp",EDGE,"E5.6.0.0"),sQuery(id+"F0.wireOp",EDGE,"E5.6.1.0"),sQuery(id+"F0.wireOp",EDGE,"E5.6.2.0"),sQuery(id+"F0.wireOp",EDGE,"E5.6.3.0"),sQuery(id+"F0.wireOp",EDGE,"E5.6.7.0"),sQuery(id+"F0.wireOp",EDGE,"E5.6.8.0"),sQuery(id+"F0.wireOp",EDGE,"E5.6.9.0"),sQuery(id+"F0.wireOp",EDGE,"E5.6.10.0"),sQuery(id+"F0.wireOp",EDGE,"E5.6.11.0"),sQuery(id+"F0.wireOp",EDGE,"E5.6.12.0"),sQuery(id+"F0.wireOp",EDGE,"E5.6.16.0"),sQuery(id+"F0.wireOp",EDGE,"E5.6.17.0"),sQuery(id+"F0.wireOp",EDGE,"E5.6.18.0"),sQuery(id+"F0.wireOp",EDGE,"E5.7.0.0"),sQuery(id+"F0.wireOp",EDGE,"E5.7.1.0"),sQuery(id+"F0.wireOp",EDGE,"E5.7.2.0"),sQuery(id+"F0.wireOp",EDGE,"E5.7.3.0"),sQuery(id+"F0.wireOp",EDGE,"E5.7.4.0"),sQuery(id+"F0.wireOp",EDGE,"E5.7.5.0"),sQuery(id+"F0.wireOp",EDGE,"E5.7.6.0"),sQuery(id+"F0.wireOp",EDGE,"E5.7.7.0"),sQuery(id+"F0.wireOp",EDGE,"E5.7.8.0"),sQuery(id+"F0.wireOp",EDGE,"E5.7.9.0"),sQuery(id+"F0.wireOp",EDGE,"E5.7.10.0"),sQuery(id+"F0.wireOp",EDGE,"E5.7.11.0"),sQuery(id+"F0.wireOp",EDGE,"E5.7.12.0"),sQuery(id+"F0.wireOp",EDGE,"E5.7.13.0"),sQuery(id+"F0.wireOp",EDGE,"E5.7.14.0"),sQuery(id+"F0.wireOp",EDGE,"E5.7.15.0"),sQuery(id+"F0.wireOp",EDGE,"E5.7.16.0"),sQuery(id+"F0.wireOp",EDGE,"E5.7.17.0"),sQuery(id+"F0.wireOp",EDGE,"E5.7.18.0"),sQuery(id+"F0.wireOp",EDGE,"E5.8.0.0"),sQuery(id+"F0.wireOp",EDGE,"E5.8.1.0"),sQuery(id+"F0.wireOp",EDGE,"E5.8.2.0"),sQuery(id+"F0.wireOp",EDGE,"E5.8.3.0"),sQuery(id+"F0.wireOp",EDGE,"E5.8.4.0"),sQuery(id+"F0.wireOp",EDGE,"E5.8.5.0"),sQuery(id+"F0.wireOp",EDGE,"E5.8.6.0"),sQuery(id+"F0.wireOp",EDGE,"E5.8.7.0"),sQuery(id+"F0.wireOp",EDGE,"E5.8.8.0"),sQuery(id+"F0.wireOp",EDGE,"E5.8.9.0"),sQuery(id+"F0.wireOp",EDGE,"E5.8.10.0"),sQuery(id+"F0.wireOp",EDGE,"E5.8.11.0"),sQuery(id+"F0.wireOp",EDGE,"E5.8.12.0"),sQuery(id+"F0.wireOp",EDGE,"E5.8.13.0"),sQuery(id+"F0.wireOp",EDGE,"E5.8.14.0"),sQuery(id+"F0.wireOp",EDGE,"E5.8.15.0"),sQuery(id+"F0.wireOp",EDGE,"E5.8.16.0"),sQuery(id+"F0.wireOp",EDGE,"E5.8.17.0"),sQuery(id+"F0.wireOp",EDGE,"E5.8.18.0"),sQuery(id+"F0.wireOp",EDGE,"E5.9.0.0"),sQuery(id+"F0.wireOp",EDGE,"E5.9.1.0"),sQuery(id+"F0.wireOp",EDGE,"E5.9.2.0"),sQuery(id+"F0.wireOp",EDGE,"E5.9.3.0"),sQuery(id+"F0.wireOp",EDGE,"E5.9.4.0"),sQuery(id+"F0.wireOp",EDGE,"E5.9.5.0"),sQuery(id+"F0.wireOp",EDGE,"E5.9.6.0"),sQuery(id+"F0.wireOp",EDGE,"E5.9.7.0"),sQuery(id+"F0.wireOp",EDGE,"E5.9.8.0"),sQuery(id+"F0.wireOp",EDGE,"E5.9.9.0"),sQuery(id+"F0.wireOp",EDGE,"E5.9.10.0"),sQuery(id+"F0.wireOp",EDGE,"E5.9.11.0"),sQuery(id+"F0.wireOp",EDGE,"E5.9.12.0"),sQuery(id+"F0.wireOp",EDGE,"E5.9.13.0"),sQuery(id+"F0.wireOp",EDGE,"E5.9.14.0"),sQuery(id+"F0.wireOp",EDGE,"E5.9.15.0"),sQuery(id+"F0.wireOp",EDGE,"E5.9.16.0"),sQuery(id+"F0.wireOp",EDGE,"E5.9.17.0"),sQuery(id+"F0.wireOp",EDGE,"E5.9.18.0"),sQuery(id+"F0.wireOp",EDGE,"E5.10.0.0"),sQuery(id+"F0.wireOp",EDGE,"E5.10.1.0"),sQuery(id+"F0.wireOp",EDGE,"E5.10.2.0"),sQuery(id+"F0.wireOp",EDGE,"E5.10.3.0"),sQuery(id+"F0.wireOp",EDGE,"E5.10.4.0"),sQuery(id+"F0.wireOp",EDGE,"E5.10.5.0"),sQuery(id+"F0.wireOp",EDGE,"E5.10.6.0"),sQuery(id+"F0.wireOp",EDGE,"E5.10.7.0"),sQuery(id+"F0.wireOp",EDGE,"E5.10.8.0"),sQuery(id+"F0.wireOp",EDGE,"E5.10.9.0"),sQuery(id+"F0.wireOp",EDGE,"E5.10.10.0"),sQuery(id+"F0.wireOp",EDGE,"E5.10.11.0"),sQuery(id+"F0.wireOp",EDGE,"E5.10.12.0"),sQuery(id+"F0.wireOp",EDGE,"E5.10.13.0"),sQuery(id+"F0.wireOp",EDGE,"E5.10.14.0"),sQuery(id+"F0.wireOp",EDGE,"E5.10.15.0"),sQuery(id+"F0.wireOp",EDGE,"E5.10.16.0"),sQuery(id+"F0.wireOp",EDGE,"E5.10.17.0"),sQuery(id+"F0.wireOp",EDGE,"E5.10.18.0"),sQuery(id+"F0.wireOp",EDGE,"E5.11.0.0"),sQuery(id+"F0.wireOp",EDGE,"E5.11.1.0"),sQuery(id+"F0.wireOp",EDGE,"E5.11.2.0"),sQuery(id+"F0.wireOp",EDGE,"E5.11.3.0"),sQuery(id+"F0.wireOp",EDGE,"E5.11.4.0"),sQuery(id+"F0.wireOp",EDGE,"E5.11.5.0"),sQuery(id+"F0.wireOp",EDGE,"E5.11.6.0"),sQuery(id+"F0.wireOp",EDGE,"E5.11.7.0"),sQuery(id+"F0.wireOp",EDGE,"E5.11.8.0"),sQuery(id+"F0.wireOp",EDGE,"E5.11.9.0"),sQuery(id+"F0.wireOp",EDGE,"E5.11.10.0"),sQuery(id+"F0.wireOp",EDGE,"E5.11.11.0"),sQuery(id+"F0.wireOp",EDGE,"E5.11.12.0"),sQuery(id+"F0.wireOp",EDGE,"E5.11.13.0"),sQuery(id+"F0.wireOp",EDGE,"E5.11.14.0"),sQuery(id+"F0.wireOp",EDGE,"E5.11.15.0"),sQuery(id+"F0.wireOp",EDGE,"E5.11.16.0"),sQuery(id+"F0.wireOp",EDGE,"E5.11.17.0"),sQuery(id+"F0.wireOp",EDGE,"E5.11.18.0"),sQuery(id+"F0.wireOp",EDGE,"E5.12.0.0"),sQuery(id+"F0.wireOp",EDGE,"E5.12.1.0"),sQuery(id+"F0.wireOp",EDGE,"E5.12.2.0"),sQuery(id+"F0.wireOp",EDGE,"E5.12.3.0"),sQuery(id+"F0.wireOp",EDGE,"E5.12.4.0"),sQuery(id+"F0.wireOp",EDGE,"E5.12.5.0"),sQuery(id+"F0.wireOp",EDGE,"E5.12.6.0"),sQuery(id+"F0.wireOp",EDGE,"E5.12.7.0"),sQuery(id+"F0.wireOp",EDGE,"E5.12.8.0"),sQuery(id+"F0.wireOp",EDGE,"E5.12.9.0"),sQuery(id+"F0.wireOp",EDGE,"E5.12.10.0"),sQuery(id+"F0.wireOp",EDGE,"E5.12.11.0"),sQuery(id+"F0.wireOp",EDGE,"E5.12.12.0"),sQuery(id+"F0.wireOp",EDGE,"E5.12.13.0"),sQuery(id+"F0.wireOp",EDGE,"E5.12.14.0"),sQuery(id+"F0.wireOp",EDGE,"E5.12.15.0"),sQuery(id+"F0.wireOp",EDGE,"E5.12.16.0"),sQuery(id+"F0.wireOp",EDGE,"E5.12.17.0"),sQuery(id+"F0.wireOp",EDGE,"E5.12.18.0"),sQuery(id+"F0.wireOp",EDGE,"E5.13.0.0"),sQuery(id+"F0.wireOp",EDGE,"E5.13.1.0"),sQuery(id+"F0.wireOp",EDGE,"E5.13.2.0"),sQuery(id+"F0.wireOp",EDGE,"E5.13.3.0"),sQuery(id+"F0.wireOp",EDGE,"E5.13.7.0"),sQuery(id+"F0.wireOp",EDGE,"E5.13.8.0"),sQuery(id+"F0.wireOp",EDGE,"E5.13.9.0"),sQuery(id+"F0.wireOp",EDGE,"E5.13.10.0"),sQuery(id+"F0.wireOp",EDGE,"E5.13.11.0"),sQuery(id+"F0.wireOp",EDGE,"E5.13.12.0"),sQuery(id+"F0.wireOp",EDGE,"E5.13.16.0"),sQuery(id+"F0.wireOp",EDGE,"E5.13.17.0"),sQuery(id+"F0.wireOp",EDGE,"E5.13.18.0"),sQuery(id+"F0.wireOp",EDGE,"E5.14.0.0"),sQuery(id+"F0.wireOp",EDGE,"E5.14.1.0"),sQuery(id+"F0.wireOp",EDGE,"E5.14.2.0"),sQuery(id+"F0.wireOp",EDGE,"E5.14.3.0"),sQuery(id+"F0.wireOp",EDGE,"E5.14.7.0"),sQuery(id+"F0.wireOp",EDGE,"E5.14.8.0"),sQuery(id+"F0.wireOp",EDGE,"E5.14.9.0"),sQuery(id+"F0.wireOp",EDGE,"E5.14.10.0"),sQuery(id+"F0.wireOp",EDGE,"E5.14.11.0"),sQuery(id+"F0.wireOp",EDGE,"E5.14.12.0"),sQuery(id+"F0.wireOp",EDGE,"E5.14.16.0"),sQuery(id+"F0.wireOp",EDGE,"E5.14.17.0"),sQuery(id+"F0.wireOp",EDGE,"E5.14.18.0"),sQuery(id+"F0.wireOp",EDGE,"E5.15.0.0"),sQuery(id+"F0.wireOp",EDGE,"E5.15.1.0"),sQuery(id+"F0.wireOp",EDGE,"E5.15.2.0"),sQuery(id+"F0.wireOp",EDGE,"E5.15.3.0"),sQuery(id+"F0.wireOp",EDGE,"E5.15.7.0"),sQuery(id+"F0.wireOp",EDGE,"E5.15.8.0"),sQuery(id+"F0.wireOp",EDGE,"E5.15.9.0"),sQuery(id+"F0.wireOp",EDGE,"E5.15.10.0"),sQuery(id+"F0.wireOp",EDGE,"E5.15.11.0"),sQuery(id+"F0.wireOp",EDGE,"E5.15.12.0"),sQuery(id+"F0.wireOp",EDGE,"E5.15.16.0"),sQuery(id+"F0.wireOp",EDGE,"E5.15.17.0"),sQuery(id+"F0.wireOp",EDGE,"E5.15.18.0"),sQuery(id+"F0.wireOp",EDGE,"E5.16.0.0"),sQuery(id+"F0.wireOp",EDGE,"E5.16.1.0"),sQuery(id+"F0.wireOp",EDGE,"E5.16.2.0"),sQuery(id+"F0.wireOp",EDGE,"E5.16.3.0"),sQuery(id+"F0.wireOp",EDGE,"E5.16.4.0"),sQuery(id+"F0.wireOp",EDGE,"E5.16.5.0"),sQuery(id+"F0.wireOp",EDGE,"E5.16.6.0"),sQuery(id+"F0.wireOp",EDGE,"E5.16.7.0"),sQuery(id+"F0.wireOp",EDGE,"E5.16.8.0"),sQuery(id+"F0.wireOp",EDGE,"E5.16.9.0"),sQuery(id+"F0.wireOp",EDGE,"E5.16.10.0"),sQuery(id+"F0.wireOp",EDGE,"E5.16.11.0"),sQuery(id+"F0.wireOp",EDGE,"E5.16.12.0"),sQuery(id+"F0.wireOp",EDGE,"E5.16.13.0"),sQuery(id+"F0.wireOp",EDGE,"E5.16.14.0"),sQuery(id+"F0.wireOp",EDGE,"E5.16.15.0"),sQuery(id+"F0.wireOp",EDGE,"E5.16.16.0"),sQuery(id+"F0.wireOp",EDGE,"E5.16.17.0"),sQuery(id+"F0.wireOp",EDGE,"E5.16.18.0"),sQuery(id+"F0.wireOp",EDGE,"E5.17.0.0"),sQuery(id+"F0.wireOp",EDGE,"E5.17.1.0"),sQuery(id+"F0.wireOp",EDGE,"E5.17.2.0"),sQuery(id+"F0.wireOp",EDGE,"E5.17.3.0"),sQuery(id+"F0.wireOp",EDGE,"E5.17.4.0"),sQuery(id+"F0.wireOp",EDGE,"E5.17.5.0"),sQuery(id+"F0.wireOp",EDGE,"E5.17.6.0"),sQuery(id+"F0.wireOp",EDGE,"E5.17.7.0"),sQuery(id+"F0.wireOp",EDGE,"E5.17.8.0"),sQuery(id+"F0.wireOp",EDGE,"E5.17.9.0"),sQuery(id+"F0.wireOp",EDGE,"E5.17.10.0"),sQuery(id+"F0.wireOp",EDGE,"E5.17.11.0"),sQuery(id+"F0.wireOp",EDGE,"E5.17.12.0"),sQuery(id+"F0.wireOp",EDGE,"E5.17.13.0"),sQuery(id+"F0.wireOp",EDGE,"E5.17.14.0"),sQuery(id+"F0.wireOp",EDGE,"E5.17.15.0"),sQuery(id+"F0.wireOp",EDGE,"E5.17.16.0"),sQuery(id+"F0.wireOp",EDGE,"E5.17.17.0"),sQuery(id+"F0.wireOp",EDGE,"E5.17.18.0"),sQuery(id+"F0.wireOp",EDGE,"E5.18.0.0"),sQuery(id+"F0.wireOp",EDGE,"E5.18.1.0"),sQuery(id+"F0.wireOp",EDGE,"E5.18.2.0"),sQuery(id+"F0.wireOp",EDGE,"E5.18.3.0"),sQuery(id+"F0.wireOp",EDGE,"E5.18.4.0"),sQuery(id+"F0.wireOp",EDGE,"E5.18.5.0"),sQuery(id+"F0.wireOp",EDGE,"E5.18.6.0"),sQuery(id+"F0.wireOp",EDGE,"E5.18.7.0"),sQuery(id+"F0.wireOp",EDGE,"E5.18.8.0"),sQuery(id+"F0.wireOp",EDGE,"E5.18.9.0"),sQuery(id+"F0.wireOp",EDGE,"E5.18.10.0"),sQuery(id+"F0.wireOp",EDGE,"E5.18.11.0"),sQuery(id+"F0.wireOp",EDGE,"E5.18.12.0"),sQuery(id+"F0.wireOp",EDGE,"E5.18.13.0"),sQuery(id+"F0.wireOp",EDGE,"E5.18.14.0"),sQuery(id+"F0.wireOp",EDGE,"E5.18.15.0"),sQuery(id+"F0.wireOp",EDGE,"E5.18.16.0"),sQuery(id+"F0.wireOp",EDGE,"E5.18.17.0"),sQuery(id+"F0.wireOp",EDGE,"E5.18.18.0"),sQuery(id+"F0.wireOp",EDGE,"8b8823dd-fd00-4bca-b446-f6f4922a5a1d.0.19.0"),sQuery(id+"F0.wireOp",EDGE,"8b8823dd-fd00-4bca-b446-f6f4922a5a1d.0.19.1"),sQuery(id+"F0.wireOp",EDGE,"8b8823dd-fd00-4bca-b446-f6f4922a5a1d.0.19.2"),sQuery(id+"F0.wireOp",EDGE,"8b8823dd-fd00-4bca-b446-f6f4922a5a1d.0.19.3"),sQuery(id+"F0.wireOp",EDGE,"8b8823dd-fd00-4bca-b446-f6f4922a5a1d.0.19.4"),sQuery(id+"F0.wireOp",EDGE,"8b8823dd-fd00-4bca-b446-f6f4922a5a1d.0.19.5"),sQuery(id+"F0.wireOp",EDGE,"8b8823dd-fd00-4bca-b446-f6f4922a5a1d.0.19.6"),sQuery(id+"F0.wireOp",EDGE,"8b8823dd-fd00-4bca-b446-f6f4922a5a1d.0.19.7"),sQuery(id+"F0.wireOp",EDGE,"8b8823dd-fd00-4bca-b446-f6f4922a5a1d.0.19.8"),sQuery(id+"F0.wireOp",EDGE,"8b8823dd-fd00-4bca-b446-f6f4922a5a1d.0.19.9"),sQuery(id+"F0.wireOp",EDGE,"8b8823dd-fd00-4bca-b446-f6f4922a5a1d.0.19.10"),sQuery(id+"F0.wireOp",EDGE,"8b8823dd-fd00-4bca-b446-f6f4922a5a1d.0.19.11"),sQuery(id+"F0.wireOp",EDGE,"8b8823dd-fd00-4bca-b446-f6f4922a5a1d.0.19.12"),sQuery(id+"F0.wireOp",EDGE,"8b8823dd-fd00-4bca-b446-f6f4922a5a1d.0.19.13"),sQuery(id+"F0.wireOp",EDGE,"8b8823dd-fd00-4bca-b446-f6f4922a5a1d.0.19.14"),sQuery(id+"F0.wireOp",EDGE,"8b8823dd-fd00-4bca-b446-f6f4922a5a1d.0.19.15"),sQuery(id+"F0.wireOp",EDGE,"8b8823dd-fd00-4bca-b446-f6f4922a5a1d.0.19.16"),sQuery(id+"F0.wireOp",EDGE,"8b8823dd-fd00-4bca-b446-f6f4922a5a1d.0.19.17"),sQuery(id+"F0.wireOp",EDGE,"8b8823dd-fd00-4bca-b446-f6f4922a5a1d.0.19.18"),sQuery(id+"F0.wireOp",EDGE,"50c97053-9d34-4ded-abf3-c7f4937d5684.0.0.19"),sQuery(id+"F0.wireOp",EDGE,"50c97053-9d34-4ded-abf3-c7f4937d5684.0.1.19"),sQuery(id+"F0.wireOp",EDGE,"50c97053-9d34-4ded-abf3-c7f4937d5684.0.2.19"),sQuery(id+"F0.wireOp",EDGE,"50c97053-9d34-4ded-abf3-c7f4937d5684.0.3.19"),sQuery(id+"F0.wireOp",EDGE,"50c97053-9d34-4ded-abf3-c7f4937d5684.0.4.19"),sQuery(id+"F0.wireOp",EDGE,"50c97053-9d34-4ded-abf3-c7f4937d5684.0.5.19"),sQuery(id+"F0.wireOp",EDGE,"50c97053-9d34-4ded-abf3-c7f4937d5684.0.6.19"),sQuery(id+"F0.wireOp",EDGE,"50c97053-9d34-4ded-abf3-c7f4937d5684.0.7.19"),sQuery(id+"F0.wireOp",EDGE,"50c97053-9d34-4ded-abf3-c7f4937d5684.0.8.19"),sQuery(id+"F0.wireOp",EDGE,"50c97053-9d34-4ded-abf3-c7f4937d5684.0.9.19"),sQuery(id+"F0.wireOp",EDGE,"50c97053-9d34-4ded-abf3-c7f4937d5684.0.10.19"),sQuery(id+"F0.wireOp",EDGE,"50c97053-9d34-4ded-abf3-c7f4937d5684.0.11.19"),sQuery(id+"F0.wireOp",EDGE,"50c97053-9d34-4ded-abf3-c7f4937d5684.0.12.19"),sQuery(id+"F0.wireOp",EDGE,"50c97053-9d34-4ded-abf3-c7f4937d5684.0.13.19"),sQuery(id+"F0.wireOp",EDGE,"50c97053-9d34-4ded-abf3-c7f4937d5684.0.14.19"),sQuery(id+"F0.wireOp",EDGE,"50c97053-9d34-4ded-abf3-c7f4937d5684.0.15.19"),sQuery(id+"F0.wireOp",EDGE,"50c97053-9d34-4ded-abf3-c7f4937d5684.0.16.19"),sQuery(id+"F0.wireOp",EDGE,"50c97053-9d34-4ded-abf3-c7f4937d5684.0.17.19"),sQuery(id+"F0.wireOp",EDGE,"50c97053-9d34-4ded-abf3-c7f4937d5684.0.18.19"),sQuery(id+"F0.wireOp",EDGE,"50c97053-9d34-4ded-abf3-c7f4937d5684.0.19.19"),sQuery(id+"F0.wireOp",EDGE,"E6"),sQuery(id+"F0.wireOp",EDGE,"E7"),sQuery(id+"F0.wireOp",EDGE,"E8"),sQuery(id+"F0.wireOp",EDGE,"E9"),sQuery(id+"F0.wireOp",EDGE,"E12"),sQuery(id+"F0.wireOp",EDGE,"E13"),sQuery(id+"F0.wireOp",EDGE,"E14"),sQuery(id+"F0.wireOp",EDGE,"E15"),sQuery(id+"F0.wireOp",EDGE,"E18"),sQuery(id+"F0.wireOp",EDGE,"E19"),sQuery(id+"F0.wireOp",EDGE,"E20"),sQuery(id+"F0.wireOp",EDGE,"E21"),sQuery(id+"F0.wireOp",EDGE,"E24"),sQuery(id+"F0.wireOp",EDGE,"E25"),sQuery(id+"F0.wireOp",EDGE,"E26"),sQuery(id+"F0.wireOp",EDGE,"E27")])],"isStart":false});
            var sketch = newSketch(context, id + "F3", { "sketchPlane" : qUnion([Q0])});
            skCircle(sketch, "E39", {"center": v(-115.87, -73.55) * mm, "radius": 5 * mm});
            skCircle(sketch, "E40", {"center": v(-115.87, -104.05) * mm, "radius": 5 * mm});
            skCircle(sketch, "E41", {"center": v(-89.87, -104.05) * mm, "radius": 5 * mm});
            skCircle(sketch, "E42", {"center": v(-89.87, -73.55) * mm, "radius": 5 * mm});
            skCircle(sketch, "E43", {"center": v(24.13, -73.55) * mm, "radius": 5 * mm});
            skCircle(sketch, "E44", {"center": v(50.13, -73.55) * mm, "radius": 5 * mm});
            skCircle(sketch, "E45", {"center": v(50.13, -104.05) * mm, "radius": 5 * mm});
            skCircle(sketch, "E46", {"center": v(24.13, -104.05) * mm, "radius": 5 * mm});
            skCircle(sketch, "E47", {"center": v(-89.87, 85.95) * mm, "radius": 5 * mm});
            skCircle(sketch, "E48", {"center": v(-89.87, 116.45) * mm, "radius": 5 * mm});
            skCircle(sketch, "E49", {"center": v(-115.87, 85.95) * mm, "radius": 5 * mm});
            skCircle(sketch, "E50", {"center": v(-115.87, 116.45) * mm, "radius": 5 * mm});
            skCircle(sketch, "E51", {"center": v(24.13, 116.45) * mm, "radius": 5 * mm});
            skCircle(sketch, "E52", {"center": v(24.13, 85.95) * mm, "radius": 5 * mm});
            skCircle(sketch, "E53", {"center": v(50.13, 116.45) * mm, "radius": 5 * mm});
            skCircle(sketch, "E54", {"center": v(50.13, 85.95) * mm, "radius": 5 * mm});
            skSolve(sketch);
        }
        {
            var Q0;
            Q0=makeQuery(id+"F3.imprint","IMPRINT",FACE,{"disambiguationData":[TD([[makeQuery(id+"F3.imprint","IMPRINT",EDGE,{"derivedFrom":sQuery(id+"F3.wireOp",EDGE,"E50")}),1.0]])]});
            var Q1;
            Q1=makeQuery(id+"F3.imprint","IMPRINT",FACE,{"disambiguationData":[TD([[makeQuery(id+"F3.imprint","IMPRINT",EDGE,{"derivedFrom":sQuery(id+"F3.wireOp",EDGE,"E48")}),1.0]])]});
            var Q2;
            Q2=makeQuery(id+"F3.imprint","IMPRINT",FACE,{"disambiguationData":[TD([[makeQuery(id+"F3.imprint","IMPRINT",EDGE,{"derivedFrom":sQuery(id+"F3.wireOp",EDGE,"E47")}),1.0]])]});
            var Q3;
            Q3=makeQuery(id+"F3.imprint","IMPRINT",FACE,{"disambiguationData":[TD([[makeQuery(id+"F3.imprint","IMPRINT",EDGE,{"derivedFrom":sQuery(id+"F3.wireOp",EDGE,"E49")}),1.0]])]});
            var Q4;
            Q4=makeQuery(id+"F3.imprint","IMPRINT",FACE,{"disambiguationData":[TD([[makeQuery(id+"F3.imprint","IMPRINT",EDGE,{"derivedFrom":sQuery(id+"F3.wireOp",EDGE,"E39")}),1.0]])]});
            var Q5;
            Q5=makeQuery(id+"F3.imprint","IMPRINT",FACE,{"disambiguationData":[TD([[makeQuery(id+"F3.imprint","IMPRINT",EDGE,{"derivedFrom":sQuery(id+"F3.wireOp",EDGE,"E40")}),1.0]])]});
            var Q6;
            Q6=makeQuery(id+"F3.imprint","IMPRINT",FACE,{"disambiguationData":[TD([[makeQuery(id+"F3.imprint","IMPRINT",EDGE,{"derivedFrom":sQuery(id+"F3.wireOp",EDGE,"E41")}),1.0]])]});
            var Q7;
            Q7=makeQuery(id+"F3.imprint","IMPRINT",FACE,{"disambiguationData":[TD([[makeQuery(id+"F3.imprint","IMPRINT",EDGE,{"derivedFrom":sQuery(id+"F3.wireOp",EDGE,"E42")}),1.0]])]});
            var Q8;
            Q8=makeQuery(id+"F3.imprint","IMPRINT",FACE,{"disambiguationData":[TD([[makeQuery(id+"F3.imprint","IMPRINT",EDGE,{"derivedFrom":sQuery(id+"F3.wireOp",EDGE,"E43")}),1.0]])]});
            var Q9;
            Q9=makeQuery(id+"F3.imprint","IMPRINT",FACE,{"disambiguationData":[TD([[makeQuery(id+"F3.imprint","IMPRINT",EDGE,{"derivedFrom":sQuery(id+"F3.wireOp",EDGE,"E46")}),1.0]])]});
            var Q10;
            Q10=makeQuery(id+"F3.imprint","IMPRINT",FACE,{"disambiguationData":[TD([[makeQuery(id+"F3.imprint","IMPRINT",EDGE,{"derivedFrom":sQuery(id+"F3.wireOp",EDGE,"E45")}),1.0]])]});
            var Q11;
            Q11=makeQuery(id+"F3.imprint","IMPRINT",FACE,{"disambiguationData":[TD([[makeQuery(id+"F3.imprint","IMPRINT",EDGE,{"derivedFrom":sQuery(id+"F3.wireOp",EDGE,"E44")}),1.0]])]});
            var Q12;
            Q12=makeQuery(id+"F3.imprint","IMPRINT",FACE,{"disambiguationData":[TD([[makeQuery(id+"F3.imprint","IMPRINT",EDGE,{"derivedFrom":sQuery(id+"F3.wireOp",EDGE,"E54")}),1.0]])]});
            var Q13;
            Q13=makeQuery(id+"F3.imprint","IMPRINT",FACE,{"disambiguationData":[TD([[makeQuery(id+"F3.imprint","IMPRINT",EDGE,{"derivedFrom":sQuery(id+"F3.wireOp",EDGE,"E52")}),1.0]])]});
            var Q14;
            Q14=makeQuery(id+"F3.imprint","IMPRINT",FACE,{"disambiguationData":[TD([[makeQuery(id+"F3.imprint","IMPRINT",EDGE,{"derivedFrom":sQuery(id+"F3.wireOp",EDGE,"E51")}),1.0]])]});
            var Q15;
            Q15=makeQuery(id+"F3.imprint","IMPRINT",FACE,{"disambiguationData":[TD([[makeQuery(id+"F3.imprint","IMPRINT",EDGE,{"derivedFrom":sQuery(id+"F3.wireOp",EDGE,"E53")}),1.0]])]});
            extrude(context, id + "F4", {"entities" : qUnion([Q0, Q1, Q2, Q3, Q4, Q5, Q6, Q7, Q8, Q9, Q10, Q11, Q12, Q13, Q14, Q15]), "operationType" : NewBodyOperationType.REMOVE, "oppositeDirection" : true, "depth" : 5 * mm});
        }
    });
